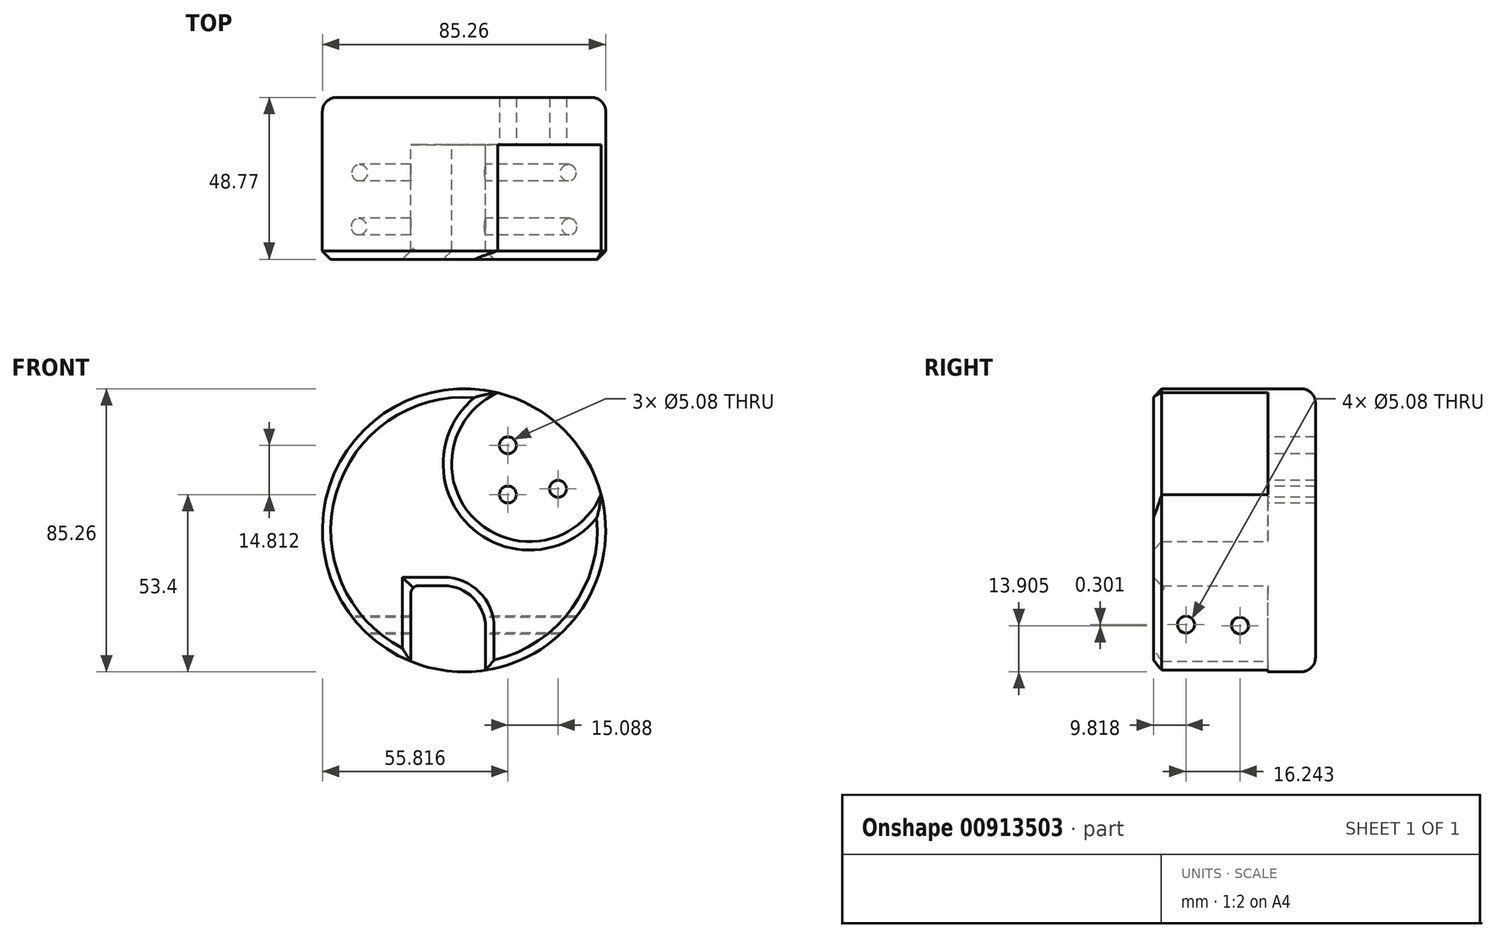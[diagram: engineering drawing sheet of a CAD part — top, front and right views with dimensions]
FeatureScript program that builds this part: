
annotation { "Feature Type Name" : "Feature", "Feature Type Description" : "" }
export const myFeature = defineFeature(function(context is Context, id is Id, definition is map)
    precondition{}
    {
        {
            var Q0;
            Q0=qCreatedBy(makeId("Front.planeOp"),FACE);
            var sketch = newSketch(context, id + "F0", { "sketchPlane" : qUnion([Q0])});
            skCircle(sketch, "E0", {"center": v(0, 0) * mm, "radius": 42.63 * mm});
            skSolve(sketch);
        }
        {
            var Q0;
            Q0=makeQuery(id+"F0.imprint","IMPRINT",FACE,{"disambiguationData":[TD([[makeQuery(id+"F0.imprint","IMPRINT",EDGE,{"derivedFrom":sQuery(id+"F0.wireOp",EDGE,"E0")}),1.0]])]});
            extrude(context, id + "F1", {"entities" : qUnion([Q0]), "depth" : 48.77 * mm, "offsetDistance" : 25.4 * mm});
        }
        {
            var Q0;
            Q0=qCreatedBy(makeId("Front.planeOp"),FACE);
            cPlane(context, id + "F2", {"entities" : qUnion([Q0]), "cplaneType" : CPlaneType.OFFSET, "offset" : 14.22 * mm, "width" : 152.4 * mm, "height" : 152.4 * mm});
        }
        {
            var Q0;
            Q0=qCreatedBy(id+"F2.planeOp",FACE);
            var sketch = newSketch(context, id + "F3", { "sketchPlane" : qUnion([Q0])});
            skCircle(sketch, "E1", {"center": v(19.7, 20) * mm, "radius": 23.44 * mm});
            skLineSegment(sketch, "E2.bottom", {"start": v(6.5, -76.45) * mm, "end": v(-16.04, -76.45) * mm});
            skLineSegment(sketch, "E2.top", {"start": v(-6.2, -16.67) * mm, "end": v(-16.04, -16.67) * mm});
            skLineSegment(sketch, "E2.left", {"start": v(6.5, -76.45) * mm, "end": v(6.5, -29.37) * mm});
            skLineSegment(sketch, "E2.right", {"start": v(-16.04, -76.45) * mm, "end": v(-16.04, -16.67) * mm});
            skLineSegment(sketch, "E3.bottom", {"start": v(-16.04, -16.67) * mm, "end": v(-61.84, -16.67) * mm});
            skLineSegment(sketch, "E3.top", {"start": v(-22.39, 8.85) * mm, "end": v(-61.84, 8.85) * mm});
            skLineSegment(sketch, "E3.left", {"start": v(-16.04, -16.67) * mm, "end": v(-16.04, 2.5) * mm});
            skLineSegment(sketch, "E3.right", {"start": v(-61.84, -16.67) * mm, "end": v(-61.84, 8.85) * mm});
            skPoint(sketch, "E4.visualSharp", {"position": v(-16.04, 8.85) * mm});
            skArc(sketch, "E4.filletArc", {"start": v(-16.04, 2.5) * mm, "mid": v(-17.9, 6.99) * mm, "end": v(-22.39, 8.85) * mm});
            skPoint(sketch, "E5.visualSharp", {"position": v(6.5, -16.67) * mm});
            skArc(sketch, "E5.filletArc", {"start": v(6.5, -29.37) * mm, "mid": v(2.78, -20.38) * mm, "end": v(-6.2, -16.67) * mm});
            skSolve(sketch);
        }
        {
            var Q0;
            Q0=makeQuery(id+"F3.imprint","IMPRINT",FACE,{"disambiguationData":[TD([[makeQuery(id+"F3.imprint","IMPRINT",EDGE,{"derivedFrom":sQuery(id+"F3.wireOp",EDGE,"E1")}),1.0]])]});
            var Q1;
            Q1=makeQuery(id+"F3.imprint","IMPRINT",FACE,{"disambiguationData":[TD([[makeQuery(id+"F3.imprint","IMPRINT",EDGE,{"derivedFrom":sQuery(id+"F3.wireOp",EDGE,"E2.bottom")}),-1.0]])]});
            extrude(context, id + "F4", {"entities" : qUnion([Q0, Q1]), "operationType" : NewBodyOperationType.REMOVE, "depth" : 44.96 * mm, "offsetDistance" : 25.4 * mm});
        }
        {
            var Q0;
            Q0=makeQuery(id+"F4.boolean.opBoolean","COPY",FACE,{"derivedFrom":makeQuery(id+"F4.opExtrude","CAP_FACE",FACE,{"disambiguationData":[OSD([sQuery(id+"F3.wireOp",EDGE,"E1")])],"isStart":true})});
            var sketch = newSketch(context, id + "F5", { "sketchPlane" : qUnion([Q0])});
            skPoint(sketch, "E6", {"position": v(13.19, 25.58) * mm});
            skPoint(sketch, "E7", {"position": v(28.27, 12.48) * mm});
            skPoint(sketch, "E8", {"position": v(13.19, 10.77) * mm});
            skSolve(sketch);
        }
        {
            var Q0;
            Q0=sQuery(id+"F5.wireOp",VERTEX,"E6");
            var Q1;
            Q1=sQuery(id+"F5.wireOp",VERTEX,"E7");
            var Q2;
            Q2=sQuery(id+"F5.wireOp",VERTEX,"E8");
            var Q3;
            Q3=makeQuery(id+"F1.opExtrude","SWEPT_BODY",BODY,{"disambiguationData":[OSD([sQuery(id+"F0.wireOp",EDGE,"E0")])]});
            hole(context, id + "F6", {"style" : HoleStyle.SIMPLE, "endStyle" : HoleEndStyle.THROUGH, "holeDiameter" : 5.08 * mm, "majorDiameter" : 6.35 * mm, "isTappedThrough" : true, "tappedDepth" : 12.7 * mm, "tapClearance" : 3, "locations" : qUnion([Q0, Q1, Q2]), "scope" : qUnion([Q3])});
        }
        {
            var Q0;
            {var subQ0=sQuery(id+"F0.wireOp",EDGE,"E0");Q0=makeQuery(id+"F4.boolean.opBoolean","SPLIT",EDGE,{"disambiguationData":[TD([makeQuery(id+"F4.opExtrude","SWEPT_FACE",FACE,{"disambiguationData":[OSD([sQuery(id+"F3.wireOp",EDGE,"E2.right")])]})])],"derivedFrom":makeQuery(id+"F1.opExtrude","CAP_EDGE",EDGE,{"disambiguationData":[OSD([subQ0])],"isStart":false})});}
            var Q1;
            Q1=makeQuery(id+"F4.boolean.opBoolean","INTERSECT",EDGE,{"derivedFrom":[makeQuery(id+"F1.opExtrude","CAP_FACE",FACE,{"disambiguationData":[OSD([sQuery(id+"F0.wireOp",EDGE,"E0")])],"isStart":false}),makeQuery(id+"F4.opExtrude","SWEPT_FACE",FACE,{"disambiguationData":[OSD([sQuery(id+"F3.wireOp",EDGE,"E1")])]})]});
            var Q2;
            Q2=makeQuery(id+"F4.boolean.opBoolean","INTERSECT",EDGE,{"derivedFrom":[makeQuery(id+"F1.opExtrude","CAP_FACE",FACE,{"disambiguationData":[OSD([sQuery(id+"F0.wireOp",EDGE,"E0")])],"isStart":false}),makeQuery(id+"F4.opExtrude","SWEPT_FACE",FACE,{"disambiguationData":[OSD([sQuery(id+"F3.wireOp",EDGE,"E2.top")])]})]});
            var Q3;
            Q3=makeQuery(id+"F4.boolean.opBoolean","INTERSECT",EDGE,{"derivedFrom":[makeQuery(id+"F1.opExtrude","CAP_FACE",FACE,{"disambiguationData":[OSD([sQuery(id+"F0.wireOp",EDGE,"E0")])],"isStart":false}),makeQuery(id+"F4.opExtrude","SWEPT_FACE",FACE,{"disambiguationData":[OSD([sQuery(id+"F3.wireOp",EDGE,"E2.right")])]})]});
            var Q4;
            {var subQ0=sQuery(id+"F0.wireOp",EDGE,"E0");Q4=makeQuery(id+"F4.boolean.opBoolean","SPLIT",EDGE,{"disambiguationData":[TD([makeQuery(id+"F4.opExtrude","SWEPT_FACE",FACE,{"disambiguationData":[OSD([sQuery(id+"F3.wireOp",EDGE,"E2.left")])]})])],"derivedFrom":makeQuery(id+"F1.opExtrude","CAP_EDGE",EDGE,{"disambiguationData":[OSD([subQ0])],"isStart":false})});}
            chamfer(context, id + "F7", {"entities" : qUnion([Q0, Q1, Q2, Q3, Q4]), "width" : 2.54 * mm, "tangentPropagation" : true});
        }
        {
            var Q0;
            Q0=makeQuery(id+"F1.opExtrude","CAP_EDGE",EDGE,{"disambiguationData":[OSD([sQuery(id+"F0.wireOp",EDGE,"E0")])],"isStart":true});
            fillet(context, id + "F8", {"entities" : qUnion([Q0]), "radius" : 4.3 * mm, "tangentPropagation" : true, "allowEdgeOverflow" : false});
        }
        {
            var Q0;
            Q0=qCreatedBy(makeId("Right.planeOp"),FACE);
            cPlane(context, id + "F9", {"entities" : qUnion([Q0]), "cplaneType" : CPlaneType.OFFSET, "offset" : 47.24 * mm, "oppositeDirection" : true, "width" : 152.4 * mm, "height" : 152.4 * mm});
        }
        {
            var Q0;
            Q0=qCreatedBy(id+"F9.planeOp",FACE);
            var sketch = newSketch(context, id + "F10", { "sketchPlane" : qUnion([Q0])});
            skPoint(sketch, "E9", {"position": v(-22.7, -28.73) * mm});
            skPoint(sketch, "E10", {"position": v(-38.95, -28.42) * mm});
            skSolve(sketch);
        }
        {
            var Q0;
            Q0=sQuery(id+"F10.wireOp",VERTEX,"E9");
            var Q1;
            Q1=sQuery(id+"F10.wireOp",VERTEX,"E10");
            var Q2;
            Q2=makeQuery(id+"F1.opExtrude","SWEPT_BODY",BODY,{"disambiguationData":[OSD([sQuery(id+"F0.wireOp",EDGE,"E0")])]});
            hole(context, id + "F11", {"style" : HoleStyle.SIMPLE, "endStyle" : HoleEndStyle.THROUGH, "oppositeDirection" : true, "holeDiameter" : 5.08 * mm, "majorDiameter" : 6.35 * mm, "isTappedThrough" : true, "tappedDepth" : 12.7 * mm, "tapClearance" : 3, "locations" : qUnion([Q0, Q1]), "scope" : qUnion([Q2])});
        }
        {
            var Q0;
            Q0=makeQuery(id+"F11.hole-1.boolean.opBoolean","INTERSECT",EDGE,{"disambiguationData":[OD(1.0)],"derivedFrom":[makeQuery(id+"F1.opExtrude","SWEPT_FACE",FACE,{"disambiguationData":[OSD([sQuery(id+"F0.wireOp",EDGE,"E0")])]}),makeQuery(id+"F11.hole-1.opRevolve","SWEPT_FACE",FACE,{"disambiguationData":[OSD([sQuery(id+"F11.hole-1.sketch.wireOp",EDGE,"core_line_2")])]})]});
            var Q1;
            Q1=makeQuery(id+"F4.boolean.opBoolean","COPY",EDGE,{"derivedFrom":makeQuery(id+"F4.opExtrude","SWEPT_EDGE",EDGE,{"disambiguationData":[OSD([sQuery(id+"F3.wireOp",EDGE,"E2.top"),sQuery(id+"F3.wireOp",EDGE,"E2.right"),sQuery(id+"F3.wireOp",EDGE,"E3.bottom"),sQuery(id+"F3.wireOp",EDGE,"E3.left")])]})});
            fillet(context, id + "F12", {"entities" : qUnion([Q0, Q1]), "radius" : 2.45 * mm, "tangentPropagation" : true, "allowEdgeOverflow" : false});
        }
    });
